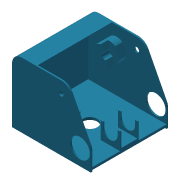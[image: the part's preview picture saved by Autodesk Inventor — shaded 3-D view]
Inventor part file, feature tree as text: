
AUTODESK INVENTOR PART (.ipt)
format: ipt  version: 2016 (Build 200138000, 138)  size: 320,000 bytes
history: native  units: in
note: dims shown in document units (in); Inventor stores cm internally (conversion verified against a paired STEP export)
features: sketch x16, extrude x15, projected_geometry x7, other x3, plane x1, mirror x1
ambient origin geometry x8: Origin, YZ Plane, XZ Plane, XY Plane, X Axis, Y Axis, Z Axis, Center Point
bodies: Solid1 (feature_tree)
feature tree (43):
  extrude  "Extrusion1"  Depth=8.0938in
  sketch  "Sketch2"  dims[d2=0.25in d3=0.0in d4=0.1562in]
  extrude  "Extrusion2"  Depth=0.1562in
  plane  "Work Plane1"
  mirror  "Mirror1"
  extrude  "Extrusion3"  Depth=6.6875in
  extrude  "Extrusion4"  Depth=2.125in
  extrude  "Extrusion5"  Depth=1.0in
  extrude  "Extrusion7"  Depth=2.0in
  sketch  "Sketch7"  dims[d14=0.1in d15=0.625in]
  other  "Work Axis1"
  sketch  "Sketch8"  dims[d16=0.15in d17=0.0in d18=3.8125in]
  other  "Work Axis2"
  sketch  "Sketch9"  dims[d19=0.0625in d20=0.0625in]
  other  "Work Axis3"
  extrude  "Extrusion8"  Depth=0.625in
  extrude  "Extrusion9"  Depth=0.15in
  extrude  "Extrusion10"  Depth=0.0625in
  sketch  "Sketch14"  dims[d29=1.5in d30=1.75in]
  extrude  "Extrusion11"  Depth=0.15in TaperAngle=0.0deg
  extrude  "Extrusion13"  Depth=0.125in
  sketch  "Sketch15"  dims[d31=0.5in d32=2.0in d33=0.0in]
  extrude  "Extrusion12"  Depth=2.0in TaperAngle=0.0deg
  extrude  "Extrusion14"  Depth=1.75in
  extrude  "Extrusion15"  Depth=2.0in TaperAngle=0.0deg
  extrude  "Extrusion16"  Depth=1.5in TaperAngle=0.0deg
  sketch  "Sketch1"  dims[d0=7.625in d1=8.0938in]
  sketch  "Sketch3"  dims[d6=1.0in d7=6.6875in]
  sketch  "Sketch4"  dims[d8=5.75in d9=2.125in]
  projected_geometry  "Projected Loop1"
  sketch  "Sketch5"  dims[d10=1.1875in d11=1.0in]
  projected_geometry  "Projected Loop2"
  sketch  "Sketch6"  dims[d12=0.5in d13=2.0in]
  projected_geometry  "Projected Loop3"
  projected_geometry  "Projected Loop4"
  sketch  "Sketch10"  dims[d21=2.5in d22=0.15in d23=0.0in]
  sketch  "Sketch11"  dims[d24=3.0in d25=0.125in]
  sketch  "Sketch12"  dims[d26=0.2188in d27=2.0in d28=0.0in]
  sketch  "Sketch16"  dims[d36=1.5in d37=0.1in d38=0.0in]
  projected_geometry  "Projected Loop5"
  sketch  "Sketch17"  dims[d39=4.0in d40=4.625in d41=4.1875in d42=2.6875in d43=3.625in d44=4.9375in d45=4.3595in d46=2.3438in d47=1.41in d48=0.3in d49=0.5in d50=0.0in d51=2.0in d52=1.5in d53=0.0in d54=2.0in d55=1.5in d56=0.0in d58=1.25in d59=0.329in d60=0.9in d61=1.5in d62=0.0in d63=1.25in d64=0.9in d65=0.329in d66=1.5in d67=0.0in d68=0.75in d69=0.0in d70=0.75in d71=0.0in d72=1.0in d73=0.75in d74=0.0in d75=1.0in d76=0.75in d77=0.0in]
  projected_geometry  "Projected Loop6"
  projected_geometry  "Projected Loop7"
